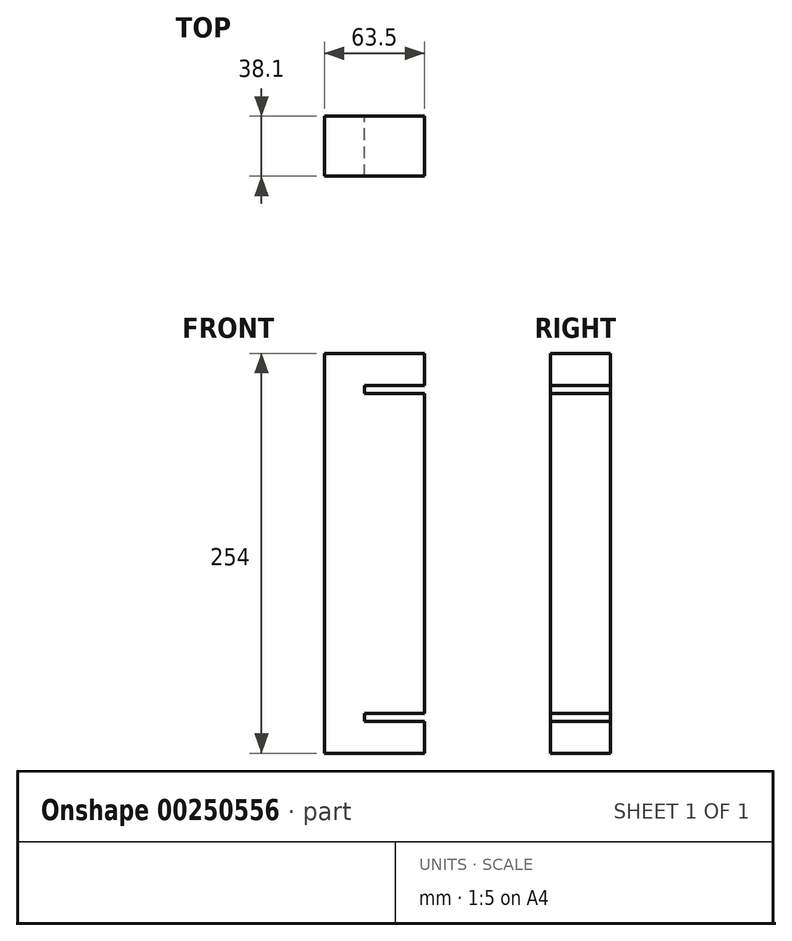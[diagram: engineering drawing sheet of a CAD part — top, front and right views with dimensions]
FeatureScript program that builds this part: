
annotation { "Feature Type Name" : "Feature", "Feature Type Description" : "" }
export const myFeature = defineFeature(function(context is Context, id is Id, definition is map)
    precondition{}
    {
        {
            var Q0;
            Q0=qCreatedBy(makeId("Front.planeOp"),FACE);
            var sketch = newSketch(context, id + "F0", { "sketchPlane" : qUnion([Q0])});
            skLineSegment(sketch, "E0.bottom", {"start": v(-36.09, 246.57) * mm, "end": v(27.41, 246.57) * mm});
            skLineSegment(sketch, "E0.top", {"start": v(-36.09, -7.43) * mm, "end": v(27.41, -7.43) * mm});
            skLineSegment(sketch, "E0.left", {"start": v(-36.09, 246.57) * mm, "end": v(-36.09, -7.43) * mm});
            skLineSegment(sketch, "E0.right", {"start": v(27.41, 246.57) * mm, "end": v(27.41, -7.43) * mm});
            skLineSegment(sketch, "E1", {"start": v(27.41, 226.2) * mm, "end": v(-10.69, 226.2) * mm});
            skLineSegment(sketch, "E2", {"start": v(-10.69, 226.2) * mm, "end": v(-10.69, 221.14) * mm});
            skLineSegment(sketch, "E3", {"start": v(-10.69, 221.14) * mm, "end": v(27.41, 221.14) * mm});
            skLineSegment(sketch, "E4", {"start": v(27.41, 17.94) * mm, "end": v(-10.69, 17.94) * mm});
            skLineSegment(sketch, "E5", {"start": v(-10.69, 17.94) * mm, "end": v(-10.69, 12.9) * mm});
            skLineSegment(sketch, "E6", {"start": v(27.41, 12.9) * mm, "end": v(-10.69, 12.9) * mm});
            skSolve(sketch);
        }
        {
            var Q0;
            {var subQ4=sQuery(id+"F0.wireOp",EDGE,"E0.bottom");Q0=makeQuery(id+"F0.imprint","IMPRINT",FACE,{"disambiguationData":[TD([[makeQuery(id+"F0.imprint","IMPRINT",EDGE,{"derivedFrom":subQ4}),-1.0]])]});}
            extrude(context, id + "F1", {"entities" : qUnion([Q0]), "depth" : 38.1 * mm});
        }
    });
